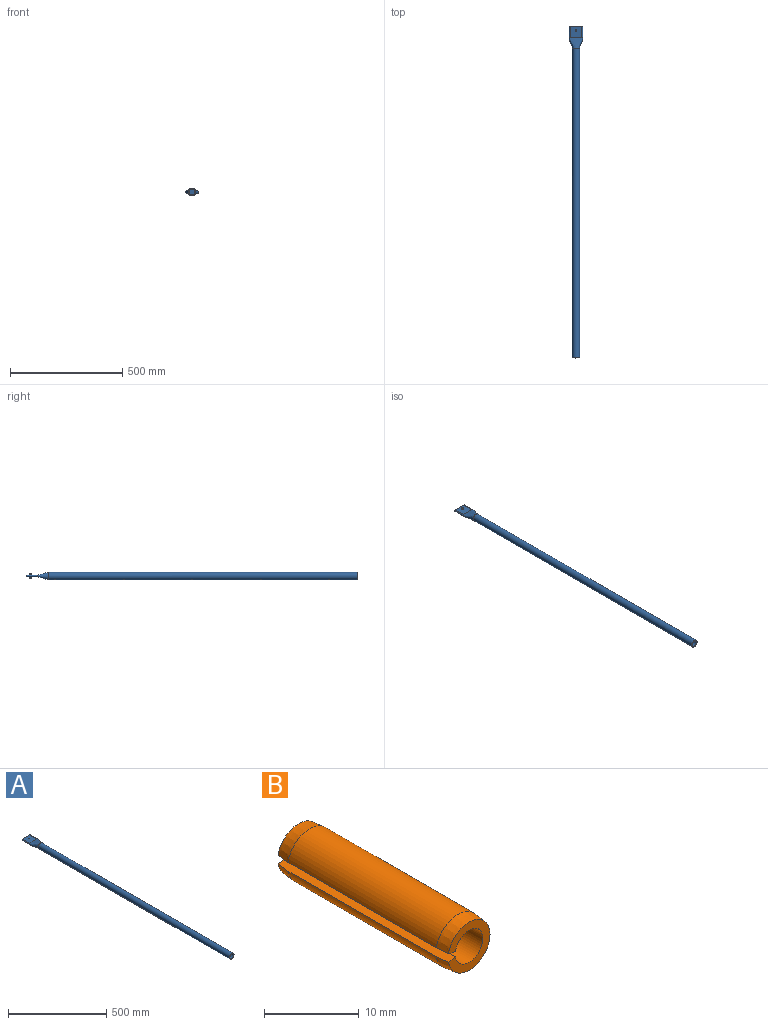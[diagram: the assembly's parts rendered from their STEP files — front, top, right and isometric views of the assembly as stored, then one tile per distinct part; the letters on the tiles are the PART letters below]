
ASSEMBLY  parts=2 mates=1
PART A: 16 faces, bbox 60x1478x33.4 mm
  f0: cylinder r=16.7mm len=1376.36mm, axis (0,-1,0), area 143779.7mm2, adj f7,f8,f11,f12,f13,f14,f15
  f1: cylinder r=13.32mm len=1376.36mm, axis (0,-1,0), area 114557mm2, adj f8,f9,f11,f12,f13,f14,f15
  f2: plane 53.29x50.8mm, normal (0,0,-1), area 2675.4mm2, adj f3,f5,f6,f7,f10
  f3: cylinder r=3.38mm len=50.8mm, axis (0,1,0), area 539.1mm2, adj f2,f4,f6,f7
  f4: plane 53.29x50.8mm, normal (0,0,1), area 2675.4mm2, adj f3,f5,f6,f7,f10
  f5: cylinder r=3.38mm len=50.8mm, axis (0,1,0), area 539.1mm2, adj f2,f4,f6,f7
  f6: plane 60.05x6.76mm, normal (0,1,0), area 395.9mm2, adj f2,f3,f4,f5
  f7: bspline ~60.05x50.8mm, area 6034.4mm2, adj f0,f2,f3,f4,f5
  f8: plane 33.4x33.4mm, normal (0,-1,0), area 318.6mm2, adj f0,f1
  f9: plane 26.64x26.64mm, normal (0,-1,0), area 557.6mm2, adj f1
  f10: cylinder r=3.17mm len=6.76mm, axis (0,0,1), area 134.8mm2, adj f2,f4
  f11: cylinder r=6.35mm len=12.7mm, axis (0,0,1), area 141.6mm2, adj f0,f1
  f12: cylinder r=6.35mm len=12.7mm, axis (0,0,1), area 141.6mm2, adj f0,f1
  f13: cylinder r=6.35mm len=12.7mm, axis (0,0,1), area 141.6mm2, adj f0,f1
  f14: cylinder r=6.35mm len=12.7mm, axis (0,0,1), area 141.6mm2, adj f0,f1
  f15: cylinder r=6.35mm len=12.7mm, axis (0,0,1), area 141.6mm2, adj f0,f1
PART B: 8 faces, bbox 6.5x25.4x6.6 mm
  f0: cone r=3.28mm half-angle=5.7deg, axis (0,-1,0), area 31.4mm2, adj f2,f3,f4,f6
  f1: cylinder r=2.06mm len=25.4mm, axis (0,1,0), area 310.1mm2, adj f2,f4,f5,f6
  f2: plane 25.4x1.2mm, normal (-0.17,0,0.98), area 30.7mm2, adj f0,f1,f3,f5,f6,f7
  f3: cylinder r=3.28mm len=22.1mm, axis (0,1,0), area 429.7mm2, adj f0,f2,f4,f7
  f4: plane 25.4x1.2mm, normal (-0.17,0,-0.98), area 30.7mm2, adj f0,f1,f3,f5,f6,f7
  f5: plane 6.22x6.18mm, normal (0,-1,0), area 16.2mm2, adj f1,f2,f4,f7
  f6: plane 6.22x6.18mm, normal (0,1,0), area 16.2mm2, adj f0,f1,f2,f4
  f7: cone r=3.11mm half-angle=5.7deg, axis (0,1,0), area 31.4mm2, adj f2,f3,f4,f5
PLACE A t=(1005.37,2091.22,3531.33)mm
PLACE B rot(axis=(1,0,0),90deg) t=(1005.37,3550.14,3531.33)mm
MATE fastened A.f10 <-> B.f1  axis (0,0,1) through (1005.37,3550.14,3531.33)mm
